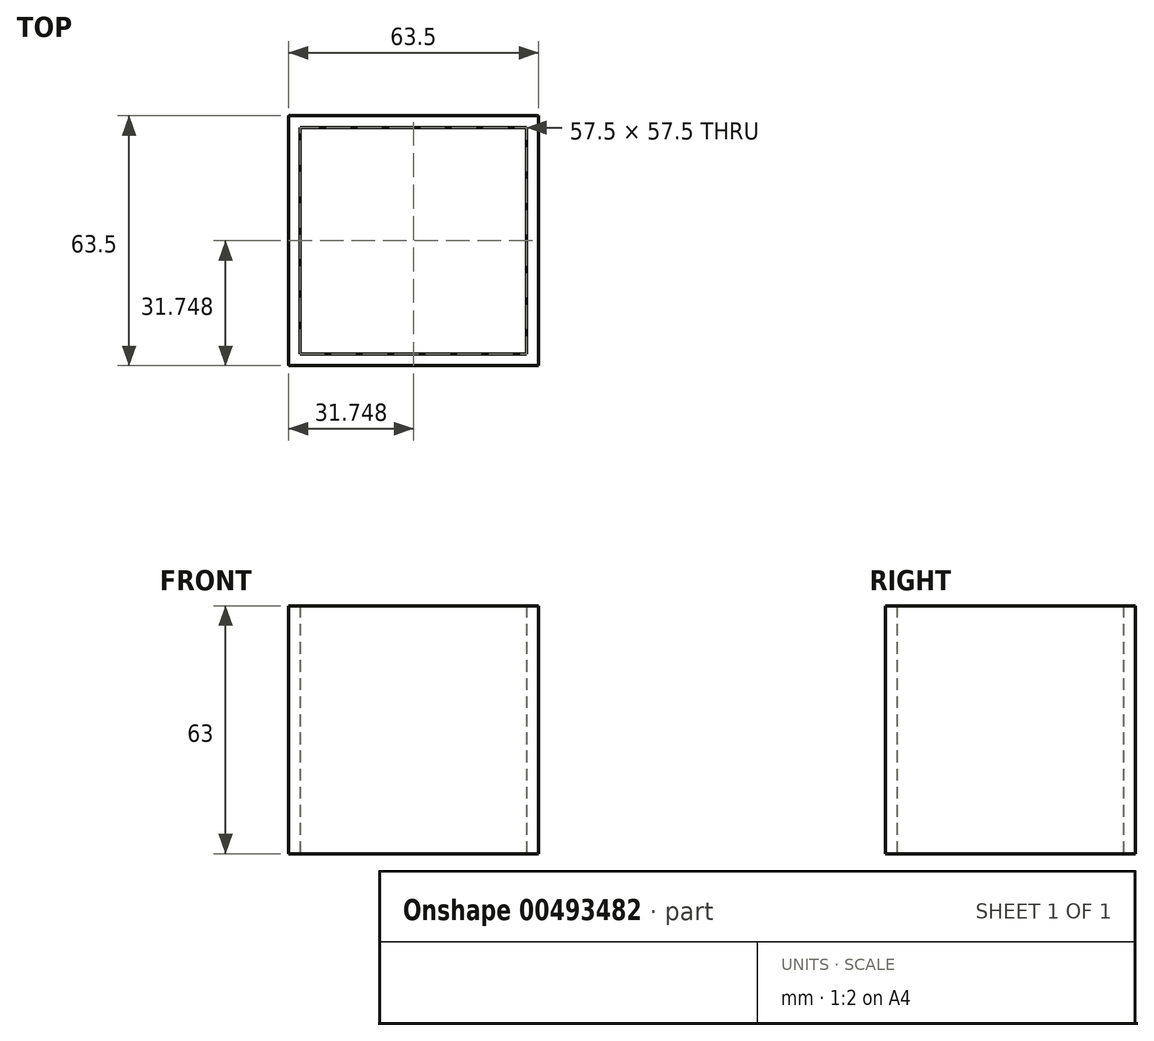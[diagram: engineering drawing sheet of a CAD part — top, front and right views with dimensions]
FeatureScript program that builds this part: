
annotation { "Feature Type Name" : "Feature", "Feature Type Description" : "" }
export const myFeature = defineFeature(function(context is Context, id is Id, definition is map)
    precondition{}
    {
        {
            var Q0;
            Q0=qCreatedBy(makeId("Top.planeOp"),FACE);
            var sketch = newSketch(context, id + "F0", { "sketchPlane" : qUnion([Q0])});
            skLineSegment(sketch, "E0.bottom", {"start": v(-24.28, 32.34) * mm, "end": v(33.22, 32.34) * mm});
            skLineSegment(sketch, "E0.top", {"start": v(-24.28, -25.16) * mm, "end": v(33.22, -25.16) * mm});
            skLineSegment(sketch, "E0.left", {"start": v(-24.28, 32.34) * mm, "end": v(-24.28, -25.16) * mm});
            skLineSegment(sketch, "E0.right", {"start": v(33.22, 32.34) * mm, "end": v(33.22, -25.16) * mm});
            skLineSegment(sketch, "E1.bottom", {"start": v(-27.28, 35.34) * mm, "end": v(36.22, 35.34) * mm});
            skLineSegment(sketch, "E1.top", {"start": v(-27.28, -28.16) * mm, "end": v(36.22, -28.16) * mm});
            skLineSegment(sketch, "E1.left", {"start": v(-27.28, 35.34) * mm, "end": v(-27.28, -28.16) * mm});
            skLineSegment(sketch, "E1.right", {"start": v(36.22, 35.34) * mm, "end": v(36.22, -28.16) * mm});
            skSolve(sketch);
        }
        {
            var Q0;
            Q0=qSketchRegion(id+"F0",true);
            extrude(context, id + "F1", {"entities" : qUnion([Q0]), "depth" : 63 * mm});
        }
    });
